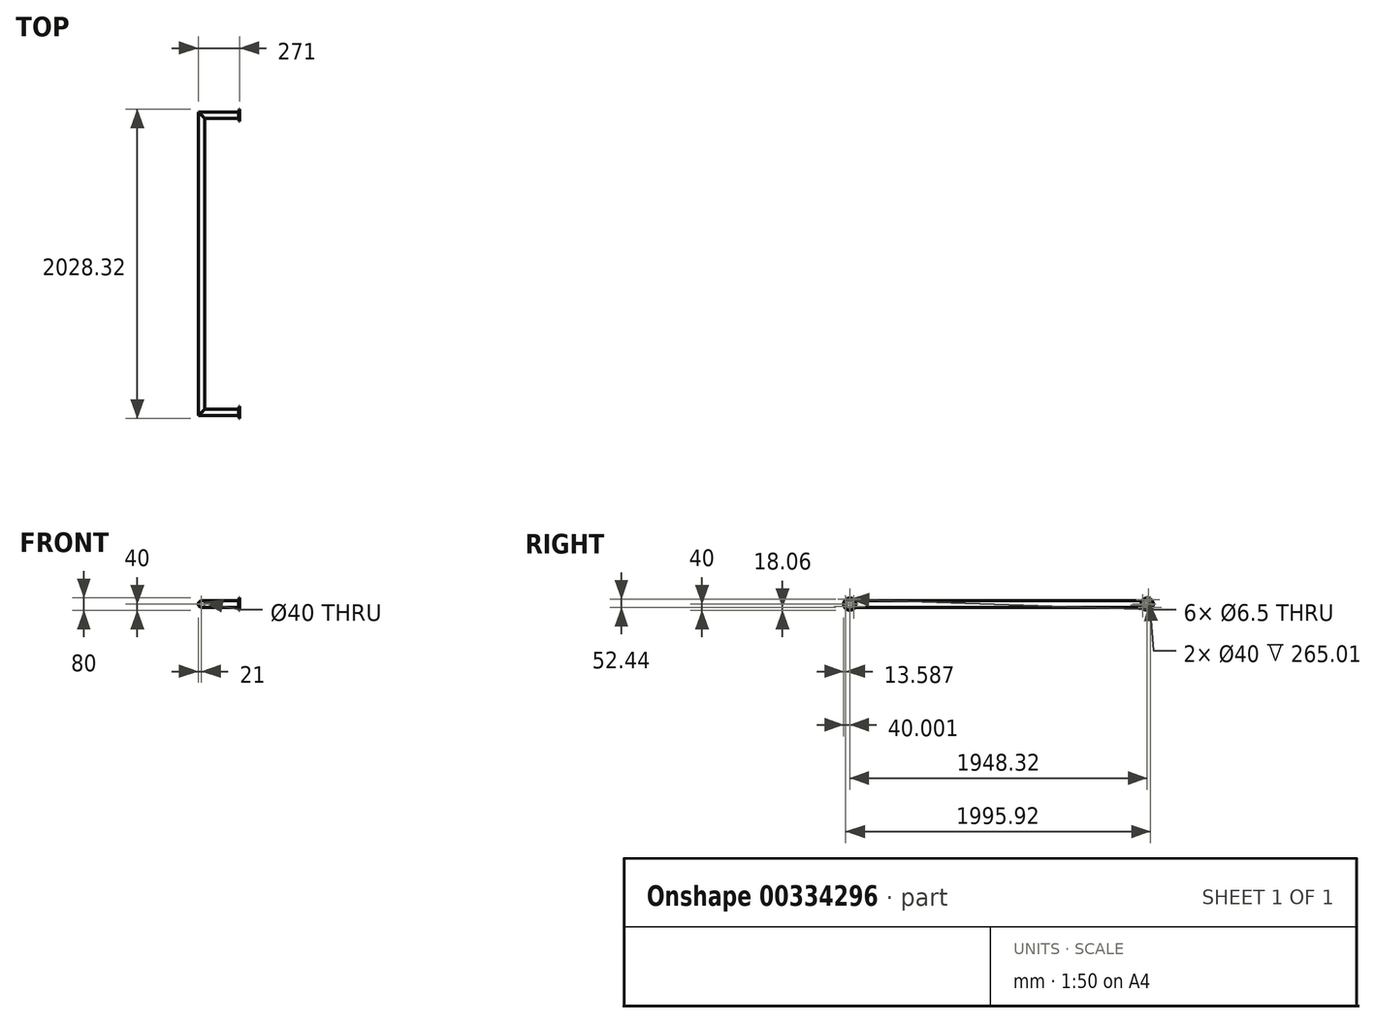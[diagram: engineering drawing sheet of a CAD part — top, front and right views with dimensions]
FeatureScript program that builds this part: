
annotation { "Feature Type Name" : "Feature", "Feature Type Description" : "" }
export const myFeature = defineFeature(function(context is Context, id is Id, definition is map)
    precondition{}
    {
        {
            var Q0;
            Q0=qCreatedBy(makeId("Right.planeOp"),FACE);
            var sketch = newSketch(context, id + "F0", { "sketchPlane" : qUnion([Q0])});
            skCircle(sketch, "E0", {"center": v(0, 0) * mm, "radius": 20 * mm});
            skCircle(sketch, "E1", {"center": v(0, 0) * mm, "radius": 21 * mm});
            skSolve(sketch);
        }
        {
            var Q0;
            Q0=qCreatedBy(makeId("Top.planeOp"),FACE);
            var sketch = newSketch(context, id + "F1", { "sketchPlane" : qUnion([Q0])});
            skLineSegment(sketch, "E2", {"start": v(0, 0) * mm, "end": v(250, 0) * mm});
            skLineSegment(sketch, "E3", {"start": v(250, 0) * mm, "end": v(250, -1948.32) * mm});
            skLineSegment(sketch, "E4", {"start": v(250, -1948.32) * mm, "end": v(0, -1948.32) * mm});
            skSolve(sketch);
        }
        {
            var Q0;
            Q0=makeQuery(id+"F0.imprint","IMPRINT",FACE,{"disambiguationData":[TD([[makeQuery(id+"F0.imprint","IMPRINT",EDGE,{"derivedFrom":sQuery(id+"F0.wireOp",EDGE,"E0")}),-1.0]])]});
            var Q1;
            Q1=sQuery(id+"F1.wireOp",EDGE,"E2");
            var Q2;
            Q2=sQuery(id+"F1.wireOp",EDGE,"E3");
            var Q3;
            Q3=sQuery(id+"F1.wireOp",EDGE,"E4");
            sweep(context, id + "F2", {"profiles" : qUnion([Q0]), "path" : qUnion([Q1, Q2, Q3])});
        }
        {
            var Q0;
            Q0=makeQuery(id+"F2.opSweep","CAP_FACE",FACE,{"disambiguationData":[OSD([sQuery(id+"F0.wireOp",EDGE,"E0"),sQuery(id+"F0.wireOp",EDGE,"E1"),sQuery(id+"F1.wireOp",VERTEX,"E4.end")])],"isStart":false});
            var sketch = newSketch(context, id + "F3", { "sketchPlane" : qUnion([Q0])});
            skCircle(sketch, "E5", {"center": v(1948.32, 0) * mm, "radius": 40 * mm});
            skLineSegment(sketch, "E6", {"start": v(1948.32, 40) * mm, "end": v(1948.32, -40) * mm, "construction": true});
            skPoint(sketch, "E7", {"position": v(1948.32, 21) * mm});
            skPoint(sketch, "E8", {"position": v(1948.32, -21) * mm});
            skPoint(sketch, "E9", {"position": v(1948.32, 30.5) * mm});
            skPoint(sketch, "E10", {"position": v(1948.32, -30.5) * mm});
            skCircle(sketch, "E11", {"center": v(0, 0) * mm, "radius": 40 * mm});
            skLineSegment(sketch, "E12", {"start": v(0, 40) * mm, "end": v(0, -40) * mm, "construction": true});
            skLineSegment(sketch, "E13", {"start": v(-15.2, 53.03) * mm, "end": v(15.2, -53.03) * mm, "construction": true});
            skPoint(sketch, "E14", {"position": v(-11.03, 38.45) * mm});
            skPoint(sketch, "E15", {"position": v(-3.3, 53.66) * mm});
            skPoint(sketch, "E16", {"position": v(-5.79, 20.19) * mm});
            skLineSegment(sketch, "E17", {"start": v(-8.4, 29.32) * mm, "end": v(-16.5, 27) * mm, "construction": true});
            skPoint(sketch, "E18", {"position": v(11.03, -38.45) * mm});
            skPoint(sketch, "E19", {"position": v(5.79, -20.19) * mm});
            skLineSegment(sketch, "E20", {"start": v(8.4, -29.32) * mm, "end": v(19.05, -26.27) * mm, "construction": true});
            skCircle(sketch, "E21", {"center": v(8.4, -29.32) * mm, "radius": 3.25 * mm, "construction": true});
            skCircle(sketch, "E22", {"center": v(-8.4, 29.32) * mm, "radius": 3.25 * mm});
            skCircle(sketch, "E23.1.0", {"center": v(-21.19, -21.94) * mm, "radius": 3.25 * mm});
            skCircle(sketch, "E23.2.0", {"center": v(29.6, -7.38) * mm, "radius": 3.25 * mm});
            skLineSegment(sketch, "E24", {"start": v(1903.57, 0) * mm, "end": v(1998.1, 0) * mm, "construction": true});
            skCircle(sketch, "E25", {"center": v(1948.32, 0) * mm, "radius": 30.5 * mm, "construction": true});
            skCircle(sketch, "E26", {"center": v(1948.32, 30.5) * mm, "radius": 3.25 * mm});
            skCircle(sketch, "E27.1.0", {"center": v(1921.9, -15.25) * mm, "radius": 3.25 * mm});
            skCircle(sketch, "E27.2.0", {"center": v(1974.73, -15.25) * mm, "radius": 3.25 * mm});
            skLineSegment(sketch, "E28", {"start": v(29.6, -7.38) * mm, "end": v(0, 0) * mm, "construction": true});
            skLineSegment(sketch, "E29", {"start": v(0, 0) * mm, "end": v(-21.19, -21.94) * mm, "construction": true});
            skSolve(sketch);
        }
        {
            var Q0;
            Q0=qSketchRegion(id+"F3",true);
            extrude(context, id + "F4", {"entities" : qUnion([Q0]), "operationType" : NewBodyOperationType.ADD, "oppositeDirection" : true, "depth" : 5 * mm});
        }
        {
            var Q0;
            Q0=makeQuery(id+"F4.boolean.opBoolean","MERGE",FACE,{"derivedFrom":[makeQuery(id+"F2.opSweep","CAP_FACE",FACE,{"disambiguationData":[OSD([sQuery(id+"F0.wireOp",EDGE,"E0"),sQuery(id+"F0.wireOp",EDGE,"E1"),sQuery(id+"F1.wireOp",VERTEX,"E2.start")])],"isStart":true}),makeQuery(id+"F4.opExtrude","CAP_FACE",FACE,{"disambiguationData":[OSD([sQuery(id+"F3.wireOp",EDGE,"E11"),sQuery(id+"F3.wireOp",EDGE,"E21"),sQuery(id+"F3.wireOp",EDGE,"E22")])],"isStart":true})]});
            cPlane(context, id + "F5", {"entities" : qUnion([Q0]), "cplaneType" : CPlaneType.OFFSET, "offset" : 25 * mm, "width" : 150 * mm, "height" : 150 * mm});
        }
        {
            var Q0;
            Q0=makeQuery(id+"F2.opSweep","SWEPT_BODY",BODY,{"disambiguationData":[OSD([sQuery(id+"F0.wireOp",EDGE,"E0"),sQuery(id+"F0.wireOp",EDGE,"E1"),sQuery(id+"F1.wireOp",EDGE,"E4")])]});
            var Q1;
            Q1=qCreatedBy(id+"F5.planeOp",FACE);
            mirror(context, id + "F6", {"operationType" : NewBodyOperationType.ADD, "entities" : qUnion([Q0]), "mirrorPlane" : qUnion([Q1])});
        }
        {
            var Q0;
            Q0=makeQuery(id+"F2.opSweep","SWEPT_BODY",BODY,{"disambiguationData":[OSD([sQuery(id+"F0.wireOp",EDGE,"E0"),sQuery(id+"F0.wireOp",EDGE,"E1"),sQuery(id+"F1.wireOp",EDGE,"E4")])]});
            deleteBodies(context, id + "F7", {"entities" : qUnion([Q0])});
        }
        {
            var Q0;
            Q0=makeQuery(id+"F6.opPattern","COPY",EDGE,{"derivedFrom":makeQuery(id+"F4.opExtrude","CAP_EDGE",EDGE,{"disambiguationData":[OSD([sQuery(id+"F3.wireOp",EDGE,"E26")])],"isStart":false}),"instanceName":"1"});
            var Q1;
            Q1=makeQuery(id+"F6.opPattern","COPY",EDGE,{"derivedFrom":makeQuery(id+"F4.opExtrude","CAP_EDGE",EDGE,{"disambiguationData":[OSD([sQuery(id+"F3.wireOp",EDGE,"E27.1.0")])],"isStart":false}),"instanceName":"1"});
            var Q2;
            Q2=makeQuery(id+"F6.opPattern","COPY",EDGE,{"derivedFrom":makeQuery(id+"F4.opExtrude","CAP_EDGE",EDGE,{"disambiguationData":[OSD([sQuery(id+"F3.wireOp",EDGE,"E27.2.0")])],"isStart":false}),"instanceName":"1"});
            var Q3;
            Q3=makeQuery(id+"F6.opPattern","COPY",EDGE,{"derivedFrom":makeQuery(id+"F4.opExtrude","CAP_EDGE",EDGE,{"disambiguationData":[OSD([sQuery(id+"F3.wireOp",EDGE,"E22")])],"isStart":false}),"instanceName":"1"});
            var Q4;
            Q4=makeQuery(id+"F6.opPattern","COPY",EDGE,{"derivedFrom":makeQuery(id+"F4.opExtrude","CAP_EDGE",EDGE,{"disambiguationData":[OSD([sQuery(id+"F3.wireOp",EDGE,"E23.2.0")])],"isStart":false}),"instanceName":"1"});
            var Q5;
            Q5=makeQuery(id+"F6.opPattern","COPY",EDGE,{"derivedFrom":makeQuery(id+"F4.opExtrude","CAP_EDGE",EDGE,{"disambiguationData":[OSD([sQuery(id+"F3.wireOp",EDGE,"E23.1.0")])],"isStart":false}),"instanceName":"1"});
            chamfer(context, id + "F8", {"entities" : qUnion([Q0, Q1, Q2, Q3, Q4, Q5]), "width" : 2 * mm, "tangentPropagation" : true});
        }
        {
            var Q0;
            Q0=makeQuery(id+"F6.opPattern","COPY",EDGE,{"derivedFrom":makeQuery(id+"F4.boolean.opBoolean","INTERSECT",EDGE,{"derivedFrom":[makeQuery(id+"F2.opSweep","SWEPT_FACE",FACE,{"disambiguationData":[OSD([sQuery(id+"F0.wireOp",EDGE,"E1"),sQuery(id+"F1.wireOp",EDGE,"E2")])]}),makeQuery(id+"F4.opExtrude","CAP_FACE",FACE,{"disambiguationData":[OSD([sQuery(id+"F3.wireOp",EDGE,"E11"),sQuery(id+"F3.wireOp",EDGE,"E22"),sQuery(id+"F3.wireOp",EDGE,"E23.1.0"),sQuery(id+"F3.wireOp",EDGE,"E23.2.0")])],"isStart":false})]}),"instanceName":"1"});
            var Q1;
            Q1=makeQuery(id+"F6.opPattern","COPY",EDGE,{"derivedFrom":makeQuery(id+"F4.boolean.opBoolean","INTERSECT",EDGE,{"derivedFrom":[makeQuery(id+"F2.opSweep","SWEPT_FACE",FACE,{"disambiguationData":[OSD([sQuery(id+"F0.wireOp",EDGE,"E1"),sQuery(id+"F1.wireOp",EDGE,"E4")])]}),makeQuery(id+"F4.opExtrude","CAP_FACE",FACE,{"disambiguationData":[OSD([sQuery(id+"F3.wireOp",EDGE,"E5"),sQuery(id+"F3.wireOp",EDGE,"E26"),sQuery(id+"F3.wireOp",EDGE,"E27.1.0"),sQuery(id+"F3.wireOp",EDGE,"E27.2.0")])],"isStart":false})]}),"instanceName":"1"});
            chamfer(context, id + "F9", {"entities" : qUnion([Q0, Q1]), "width" : 3 * mm, "tangentPropagation" : true});
        }
    });
